# Revit family: Soap_Dish-Grohe-Selection_Cube-40809_Series
name_source: partatom
category: Specialty Equipment
revit_build: Autodesk Revit 2018 (Build: 20170223_1515(x64)
units: mm (PartAtom-declared; Revit-internal decimal feet)

## family parameters
Cut with Voids When Loaded = No
Host = Face
OmniClass Number = 23.40.20.21.34
OmniClass Title = Soap Holders, Dispensers
Part Type = Normal
Room Calculation Point = No
Round Connector Dimension = Use Diameter
Shared = Yes

## types (1)
- 40809000
    Assembly Code = C1030200
    Default Elevation = 43"
    Description = Selection Cube Corner shelf
    Finish = Metal-Grohe-000-StarLight Chrome
    Height = 1 5/8"
    Installation Type = Wall Mounted
    Length = 7 7/8"
    Manufacturer = Grohe
    Material = Metal-Grohe-000-StarLight Chrome
    Model = 40809000
    Price = Prices may vary. Please consult Manufacturer Representative for most up-to-date price list.
    Product Page URL = https://www.grohe.us
    Revised Date = 05/28/2021
    URL = https://www.grohe.us
    Width = 7 7/8"

## geometry (parser evidence)
native form markers: Sweep x2
no freeform markers — native parametric forms only
